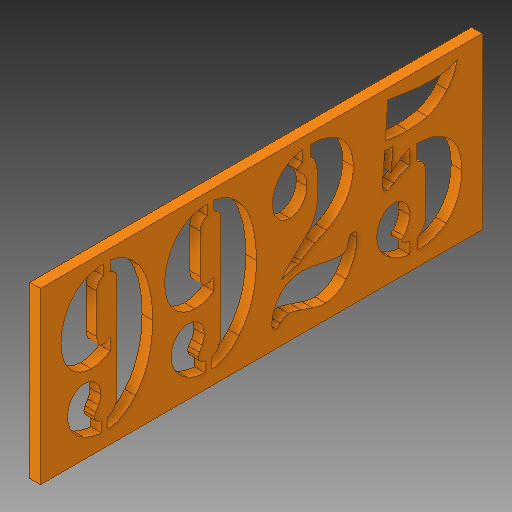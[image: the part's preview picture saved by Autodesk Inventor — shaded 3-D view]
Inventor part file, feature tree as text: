
AUTODESK INVENTOR PART (.ipt)
format: ipt  version: 2019 (Build 230136000, 136)  size: 473,600 bytes
history: native  units: in
note: dims shown in document units (in); Inventor stores cm internally (conversion verified against a paired STEP export)
features: extrude x2, thicken_offset x2, sketch x2, projected_geometry x1
ambient origin geometry x8: Origin, YZ Plane, XZ Plane, XY Plane, X Axis, Y Axis, Z Axis, Center Point
bodies: Solid1 (feature_tree)
feature tree (7):
  extrude  "Extrusion1"  Depth=8.5in
  extrude  "Extrusion3"  Depth=0.25in TaperAngle=0.0deg
  thicken_offset  "Thicken1"
  thicken_offset  "Thicken2"
  sketch  "Sketch1"  dims[d0=3.0in d1=8.5in]
  sketch  "Sketch2"  dims[d2=0.1875in d3=0.0in d9=0.25in d10=0.0in d13=0.35in d14=0.35in d15=0.35in d16=0.35in]
  projected_geometry  "Projected Loop1"
